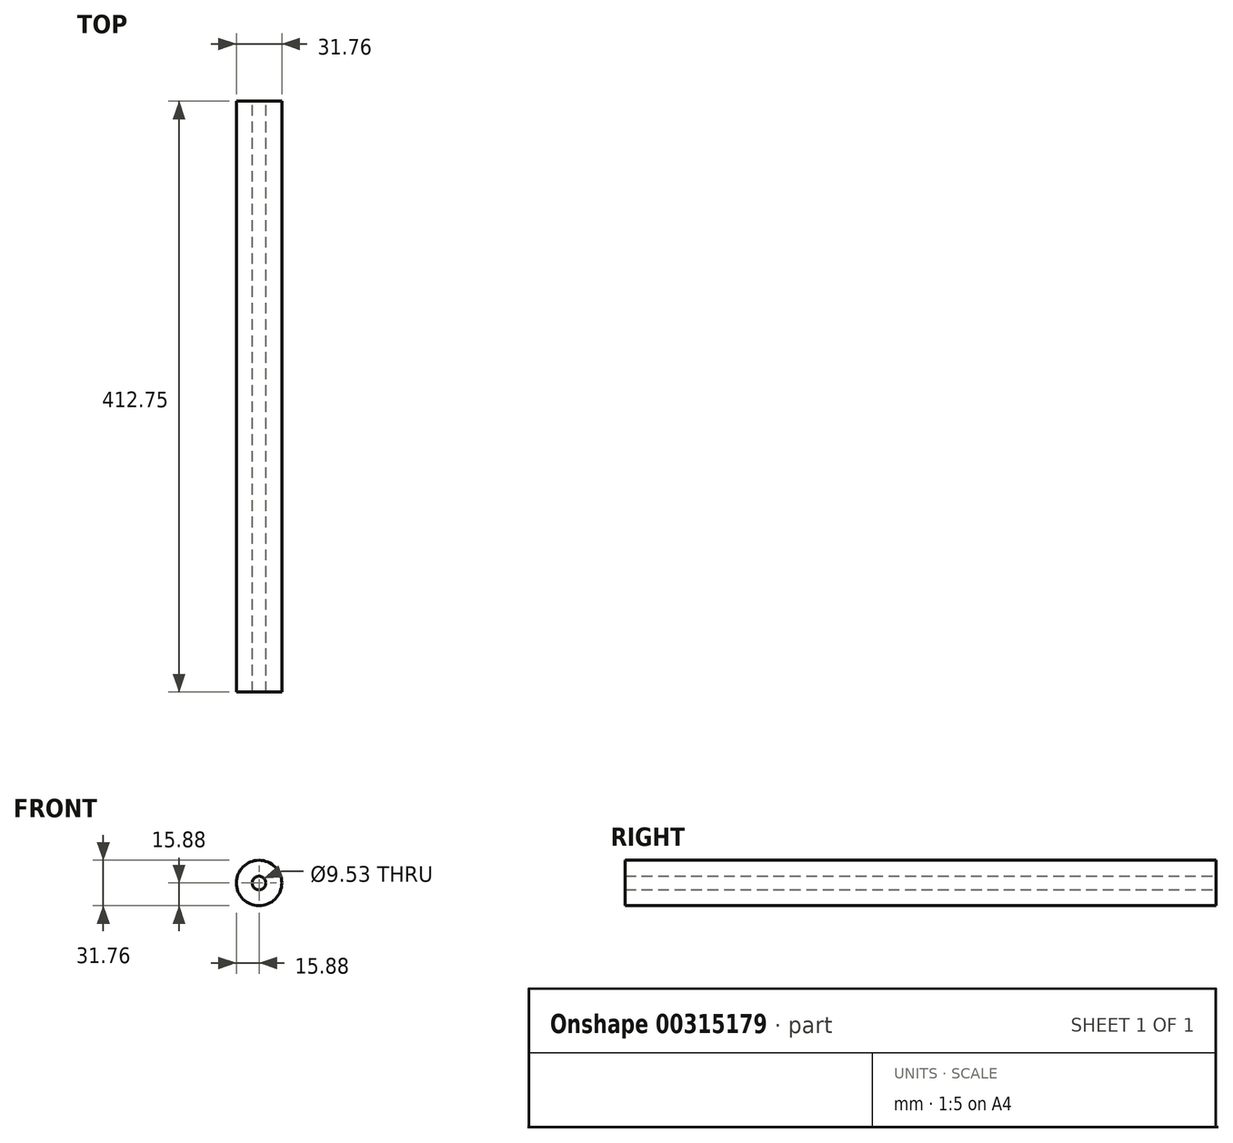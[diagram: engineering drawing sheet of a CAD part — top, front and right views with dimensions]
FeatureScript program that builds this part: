
annotation { "Feature Type Name" : "Feature", "Feature Type Description" : "" }
export const myFeature = defineFeature(function(context is Context, id is Id, definition is map)
    precondition{}
    {
        {
            var Q0;
            Q0=qCreatedBy(makeId("Front.planeOp"),FACE);
            var sketch = newSketch(context, id + "F0", { "sketchPlane" : qUnion([Q0])});
            skCircle(sketch, "E0", {"center": v(0, 0) * mm, "radius": 15.88 * mm});
            skCircle(sketch, "E1", {"center": v(0, 0) * mm, "radius": 4.76 * mm});
            skSolve(sketch);
        }
        {
            var Q0;
            Q0 = qSketchRegion(id + "F0", true);
            extrude(context, id + "F1", {"entities" : qUnion([Q0]), "depth" : 412.75 * mm});
        }
    });
